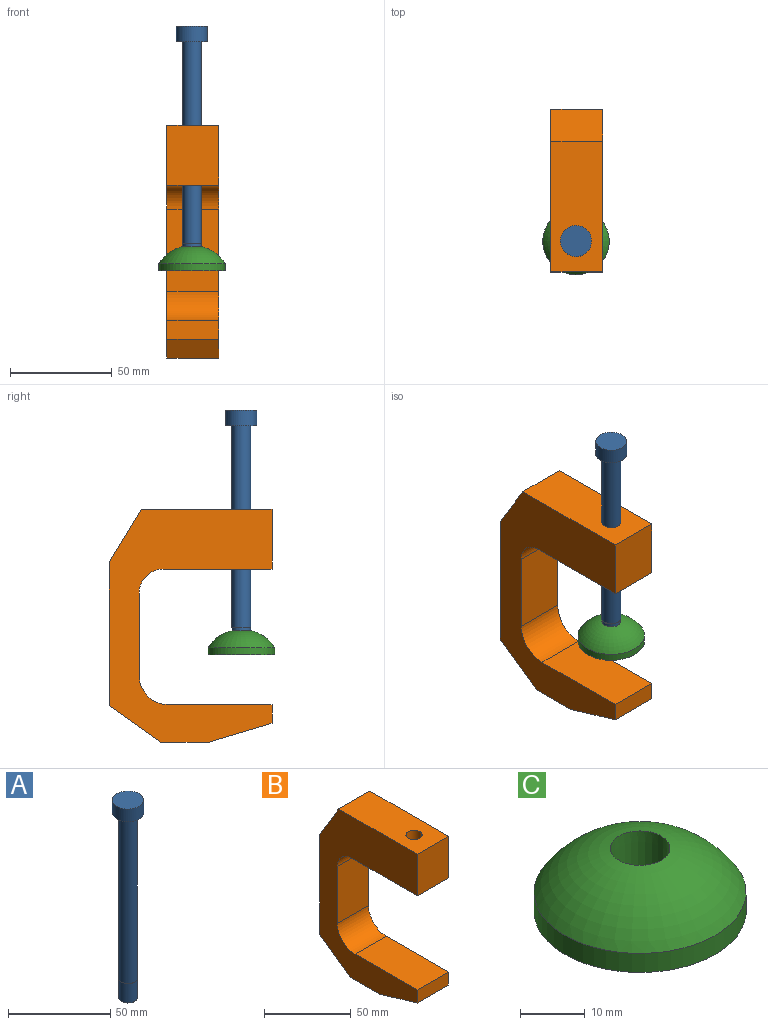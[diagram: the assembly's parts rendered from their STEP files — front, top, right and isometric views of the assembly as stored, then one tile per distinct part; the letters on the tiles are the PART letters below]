
ASSEMBLY  parts=3 mates=2
PART A: 7 faces, bbox 15.3x15.3x118.4 mm
  f0: cylinder r=7.65mm len=15.31mm, axis (0,0,-1), area 366.4mm2, adj f1,f2
  f1: plane 15.31x15.31mm, normal (0,0,1), area 184mm2, adj f0
  f2: plane 15.31x15.31mm, normal (0,0,-1), area 116.5mm2, adj f0,f3
  f3: cylinder r=4.63mm len=99.06mm, axis (0,0,1), area 2884.7mm2, adj f2,f4
  f4: plane 9.27x9.27mm, normal (0,0,-1), area 2.5mm2, adj f3,f5
  f5: cylinder r=4.55mm len=11.68mm, axis (0,0,1), area 333.8mm2, adj f4,f6
  f6: plane 9.09x9.09mm, normal (0,0,-1), area 64.9mm2, adj f5
PART B: 16 faces, bbox 25.4x79.8x114.3 mm
  f0: plane 25.4x9.17mm, normal (0,-1,0), area 232.8mm2, adj f1,f12,f13,f14
  f1: plane 30.87x25.4mm, normal (0,-0.28,-0.96), area 818mm2, adj f0,f2,f13,f14
  f2: plane 25.4x23.71mm, normal (0,0,-1), area 602.2mm2, adj f1,f3,f13,f14
  f3: plane 25.4x25.25mm, normal (0,0.58,-0.82), area 785.4mm2, adj f2,f4,f13,f14
  f4: plane 70.62x25.4mm, normal (0,1,0), area 1793.7mm2, adj f3,f5,f13,f14
  f5: plane 25.83x25.4mm, normal (0,0.85,0.52), area 767.5mm2, adj f4,f6,f13,f14
  f6: plane 64.16x25.4mm, normal (0,0,1), area 1562.1mm2, adj f5,f7,f13,f14,f15
  f7: plane 29.4x25.4mm, normal (0,-1,0), area 746.8mm2, adj f6,f8,f13,f14
  f8: plane 53.49x25.4mm, normal (0,0,-1), area 1291.2mm2, adj f7,f9,f13,f14,f15
  f9: cylinder r=11.8mm len=25.4mm, axis (-1,0,0), area 470.8mm2, adj f8,f10,f13,f14
  f10: plane 40.34x25.4mm, normal (0,-1,0), area 1024.6mm2, adj f9,f11,f13,f14
  f11: cylinder r=14.43mm len=25.4mm, axis (-1,0,0), area 575.6mm2, adj f10,f12,f13,f14
  f12: plane 50.87x25.4mm, normal (0,0,1), area 1292mm2, adj f0,f11,f13,f14
  f13: plane 114.3x79.83mm, normal (1,0,0), area 4283.7mm2, adj f0,f1,f2,f3,f4,f5,f6,f7
  f14: plane 114.3x79.83mm, normal (-1,0,0), area 4283.7mm2, adj f0,f1,f2,f3,f4,f5,f6,f7
  f15: cylinder r=4.64mm len=29.4mm, axis (0,0,1), area 856.4mm2, adj f6,f8
PART C: 5 faces, bbox 32.6x32.6x11.9 mm
  f0: cone r=4.59mm half-angle=0.6deg, axis (0,0,1), area 237mm2, adj f1,f4
  f1: cylinder r=4.5mm len=8.99mm, axis (0,0,1), area 101.4mm2, adj f0,f2
  f2: plane 32.64x32.64mm, normal (0,0,-1), area 773.1mm2, adj f1,f3
  f3: cylinder r=16.32mm len=32.64mm, axis (0,0,1), area 368mm2, adj f2,f4
  f4: torus R=0.76mm, axis (0,0,1), area 1022.7mm2, adj f0,f3
PLACE A rot(axis=(0,0,1),3.6deg) t=(52.28,-33.49,84.45)mm
PLACE B t=(-11.79,-2.3,-3.22)mm fixed
PLACE C t=(0.56,-89.53,6.43)mm
MATE cylindrical A.f0 <-> B.f15  axis (0,0,1) through (0.56,-33.54,34.92)mm
MATE revolute A.f0 <-> C.f0  axis (0,0,1) through (0.56,-33.54,-20.46)mm
